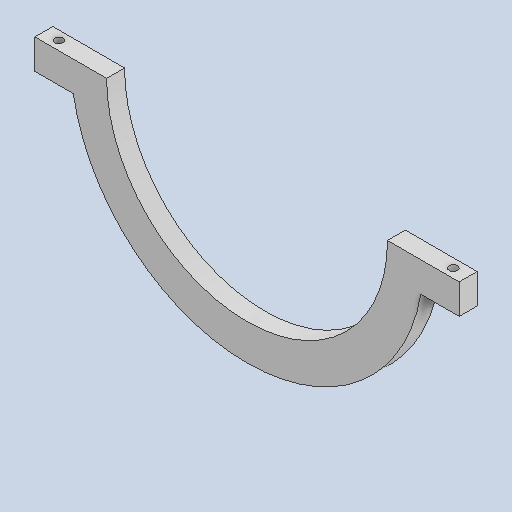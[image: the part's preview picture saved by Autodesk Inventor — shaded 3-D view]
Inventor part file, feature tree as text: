
AUTODESK INVENTOR PART (.ipt)
format: ipt  version: 2025 (Build 290162010, 162A)  size: 183,808 bytes
history: native  units: mm
features: sketch x4, hole x3, extrude x1, fillet x1, pattern_circular x1, mirror x1, other x1
ambient origin geometry x8: Origin, YZ Plane, XZ Plane, XY Plane, X Axis, Y Axis, Z Axis, Center Point
bodies: Solid1 (feature_tree)
feature tree (12):
  extrude  "Extrusion1"  Depth=30.0mm
  sketch  "Sketch4"  dims[d27=265.0mm d35=1.963495mm]
  sketch  "Sketch7"  dims[d36=60.0mm d40=60.0mm d41=50.0mm]
  fillet  "Fillet2"  Radius=80.0mm
  hole  "Hole1"  [1 undecoded]
  hole  "Hole2"  [1 undecoded]
  pattern_circular  "Circular Pattern4"  Count=5  [1 undecoded]
  hole  "Hole3"  [1 undecoded]
  mirror  "Mirror1"
  sketch  "Sketch1"  dims[d2=30.0mm d3=0.0mm d13=530.0mm d26=80.0mm]
  sketch  "Sketch8"  dims[d42=25.0mm d46=14.0mm d47=32.0mm d48=24.0mm d49=15.0mm d50=90.0deg d51=8.0mm d52=20.594885mm d53=14.0mm d54=6.0mm d55=24.0mm d56=15.0mm d57=90.0deg d58=8.0mm d59=20.594885mm d60=90.0mm d61=180.0deg d63=25.0mm d64=14.0mm d65=6.0mm d66=4.0mm d67=2.0mm d68=90.0deg d69=8.0mm d70=20.594885mm d71=10.0mm]
  other  "Definition1"
note: 4 required parameter values undecoded (feature->parameter linkage not recoverable at this tier; creation-order binding heuristic only, values carry confidence <= 0.55)
